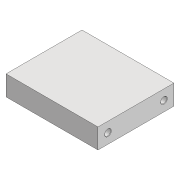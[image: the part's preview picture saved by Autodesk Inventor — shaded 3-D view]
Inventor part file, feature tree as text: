
AUTODESK INVENTOR PART (.ipt)
format: ipt  version: 2022 (Build 260153000, 153)  size: 99,328 bytes
history: native  units: mm
features: sketch x2, other x1, extrude x1, hole x1, chamfer x1
ambient origin geometry x8: Origin, YZ Plane, XZ Plane, XY Plane, X Axis, Y Axis, Z Axis, Center Point
bodies: Body1 (feature_tree)
feature tree (6):
  other  "Твердое тело1"
  extrude  "Выдавливание1"  Depth=10.0mm
  hole  "Отверстие1"  [1 undecoded]
  chamfer  "Фаска1"  Distance=46.0mm
  sketch  "Эскиз1"
  sketch  "Эскиз2"
note: 1 required parameter value undecoded (feature->parameter linkage not recoverable at this tier; creation-order binding heuristic only, values carry confidence <= 0.55)
